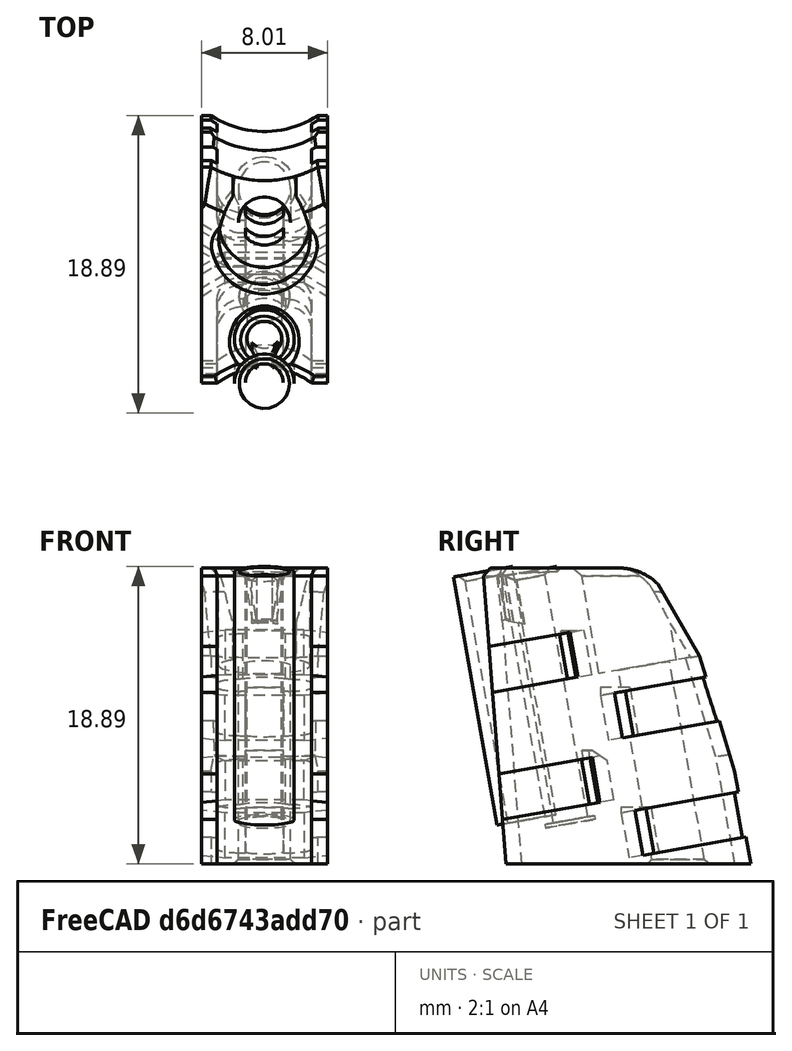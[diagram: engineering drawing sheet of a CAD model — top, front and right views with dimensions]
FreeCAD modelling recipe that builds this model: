
FCSTD DOCUMENT  (FreeCAD 0.18R14555 (Git shallow))
Label: cable-support-175
License: All rights reserved
LicenseURL: http://en.wikipedia.org/wiki/All_rights_reserved
objects: Part::Feature×4, Part::Cylinder×4, Part::Cut×4, Part::Chamfer×4, Part::Box×2, Part::MultiFuse×2
note: 20 computed .brp shape members not serialized (recipe doc carries the construction recipe); baked Part::Feature solids carry a one-line shape summary decoded from their .brp

FEATURE [Part::Feature] Part__Feature021001  label="part_b001"
  Placement = pos=(4.525,17.5966,-17.1984) rot=(0.57735,-0.57735,0.57735;2.0944rad)
  shape: bbox 10.15 x 17.01 x 19.47 mm, 111 faces (baked)
FEATURE [Part::Cylinder] Cylinder
  Angle = 360
  AttacherType = Attacher::AttachEngine3D
  Height = 16
  Placement = pos=(0.52,0.33,2.75) rot=(1,0,0;0.174533rad)
  Radius = 1.9
FEATURE [Part::Cylinder] Cylinder001
  Angle = 360
  AttacherType = Attacher::AttachEngine3D
  Height = 16
  Placement = pos=(0.52,0.33,2.75) rot=(1,0,0;0.174533rad)
  Radius = 1.1
FEATURE [Part::Box] Box  label="Cube"
  AttacherType = Attacher::AttachEngine3D
  Height = 4
  Length = 1
  Placement = pos=(0.05,-2.43867,15.6742) rot=(-1,0,0;0.174533rad)
  Width = 3
FEATURE [Part::Cylinder] Cylinder002
  Angle = 360
  AttacherType = Attacher::AttachEngine3D
  Height = 16
  Placement = pos=(0.52,0.33,2.75) rot=(1,0,0;0.174533rad)
  Radius = 1.9
FEATURE [Part::Cylinder] Cylinder003
  Angle = 360
  AttacherType = Attacher::AttachEngine3D
  Height = 16
  Placement = pos=(0.52,0.33,2.75) rot=(1,0,0;0.174533rad)
  Radius = 1.2
FEATURE [Part::Cut] Cut
  Base = -> Cylinder
  Tool = -> Cylinder001
FEATURE [Part::Cut] Cut001
  Base = -> Cylinder002
  Tool = -> Cylinder003
FEATURE [Part::Chamfer] Chamfer
  Base = -> Cut001
  Edges = 1 edges r=0.4: [Edge4]
FEATURE [Part::Chamfer] Chamfer001
  Base = -> Cut
  Edges = 1 edges r=0.4: [Edge4]
FEATURE [Part::Feature] Chamfer002
  Placement = pos=(0,2.8,0) rot=(0,0,1;0rad)
  shape: bbox 3.8 x 6.521 x 16.42 mm, 5 faces (baked)
FEATURE [Part::Feature] Chamfer001001  label="Chamfer003"
  Placement = pos=(0,2.8,0) rot=(0,0,1;0rad)
  shape: bbox 3.8 x 6.521 x 16.42 mm, 5 faces (baked)
FEATURE [Part::Box] Box001  label="Cube001"
  AttacherType = Attacher::AttachEngine3D
  Height = 4
  Length = 1
  Placement = pos=(0.05,-2.43867,15.6742) rot=(-1,0,0;0.174533rad)
  Width = 3
FEATURE [Part::Cut] Cut002
  Base = -> Chamfer002
  Tool = -> Box
FEATURE [Part::Cut] Cut003
  Base = -> Chamfer001001
  Tool = -> Box001
FEATURE [Part::Chamfer] Chamfer001002
  Base = -> Cut003
  Edges = 2 edges r=0.4: [Edge11,Edge18]
FEATURE [Part::Chamfer] Chamfer001003
  Base = -> Cut002
  Edges = 2 edges r=0.4: [Edge11,Edge18]
FEATURE [Part::Feature] Part__Feature021002  label="part_b002"
  Placement = pos=(4.525,17.5966,-17.1984) rot=(0.57735,-0.57735,0.57735;2.0944rad)
  shape: bbox 10.15 x 17.01 x 19.47 mm, 111 faces (baked)
FEATURE [Part::MultiFuse] Fusion
  Shapes = -> [Part__Feature021002,Chamfer001003]
FEATURE [Part::MultiFuse] Fusion001
  Shapes = -> [Chamfer001002,Part__Feature021001]
